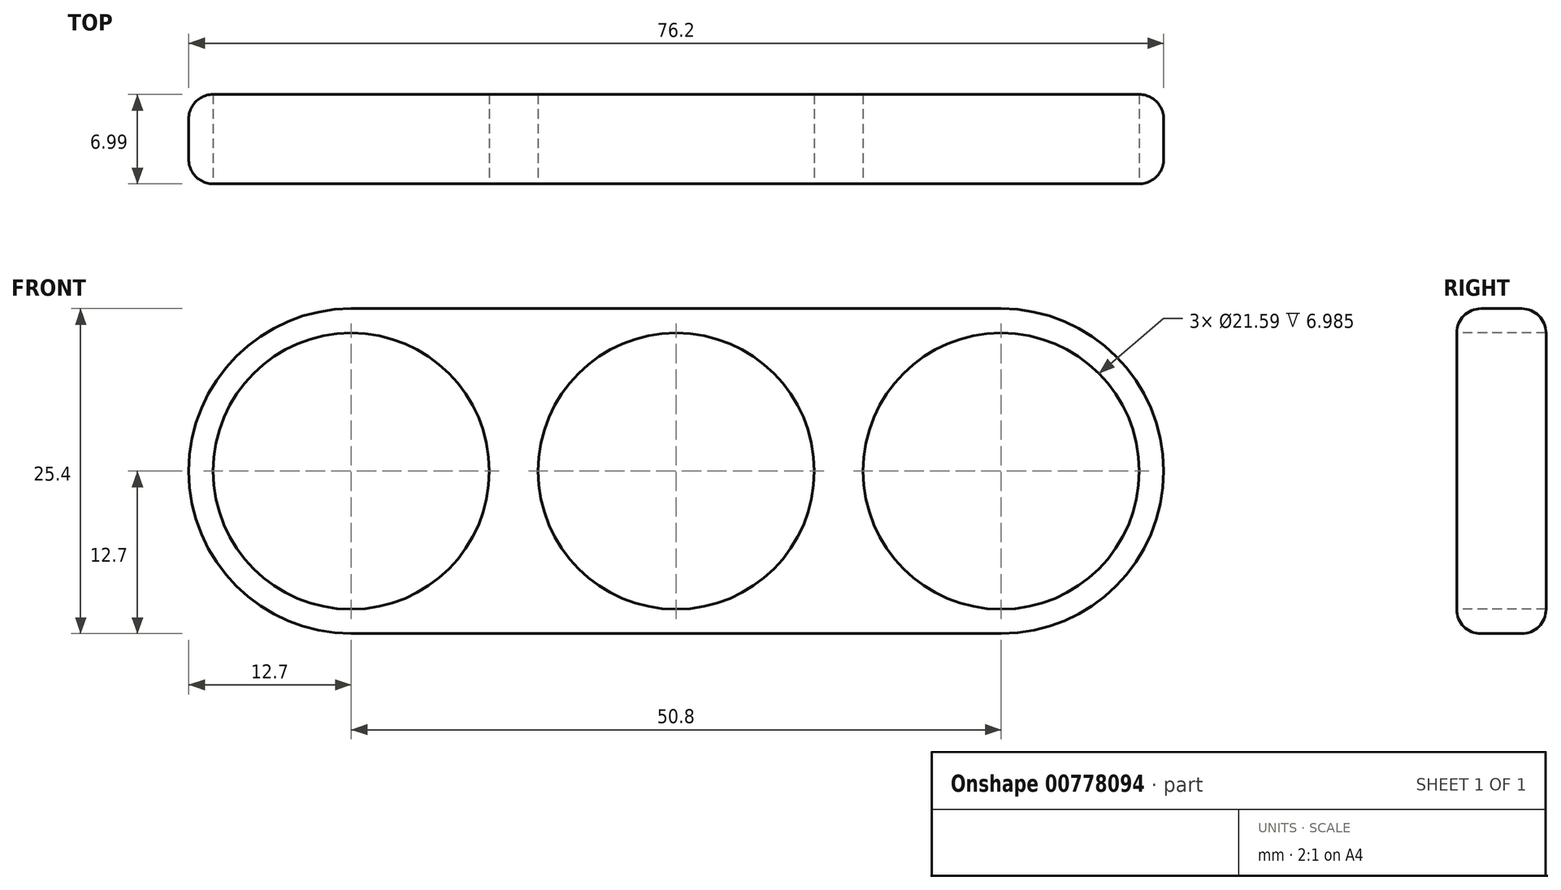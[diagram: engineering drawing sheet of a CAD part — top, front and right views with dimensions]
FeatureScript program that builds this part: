
annotation { "Feature Type Name" : "Feature", "Feature Type Description" : "" }
export const myFeature = defineFeature(function(context is Context, id is Id, definition is map)
    precondition{}
    {
        {
            var Q0;
            Q0=qCreatedBy(makeId("Front.planeOp"),FACE);
            var sketch = newSketch(context, id + "F0", { "sketchPlane" : qUnion([Q0])});
            skLineSegment(sketch, "E0", {"start": v(0, 0) * mm, "end": v(76.2, 0) * mm});
            skLineSegment(sketch, "E1", {"start": v(76.2, 0) * mm, "end": v(76.2, 25.4) * mm});
            skLineSegment(sketch, "E2", {"start": v(76.2, 25.4) * mm, "end": v(0, 25.4) * mm});
            skLineSegment(sketch, "E3", {"start": v(0, 25.4) * mm, "end": v(0, 0) * mm});
            skSolve(sketch);
        }
        {
            var Q0;
            Q0 = qSketchRegion(id + "F0", true);
            extrude(context, id + "F1", {"entities" : qUnion([Q0]), "depth" : 7 * mm, "offsetDistance" : 25.4 * mm});
        }
        {
            var Q0;
            Q0=makeQuery(id+"F1.opExtrude","SWEPT_EDGE",EDGE,{"disambiguationData":[OSD([sQuery(id+"F0.wireOp",EDGE,"E1"),sQuery(id+"F0.wireOp",EDGE,"E2")])]});
            var Q1;
            Q1=makeQuery(id+"F1.opExtrude","SWEPT_EDGE",EDGE,{"disambiguationData":[OSD([sQuery(id+"F0.wireOp",EDGE,"E2"),sQuery(id+"F0.wireOp",EDGE,"E3")])]});
            var Q2;
            Q2=makeQuery(id+"F1.opExtrude","SWEPT_EDGE",EDGE,{"disambiguationData":[OSD([sQuery(id+"F0.wireOp",EDGE,"E0"),sQuery(id+"F0.wireOp",EDGE,"E1")])]});
            var Q3;
            Q3=makeQuery(id+"F1.opExtrude","SWEPT_EDGE",EDGE,{"disambiguationData":[OSD([sQuery(id+"F0.wireOp",EDGE,"E0"),sQuery(id+"F0.wireOp",EDGE,"E3")])]});
            fillet(context, id + "F2", {"entities" : qUnion([Q0, Q1, Q2, Q3]), "radius" : 12.7 * mm, "tangentPropagation" : true, "allowEdgeOverflow" : false});
        }
        {
            var Q0;
            Q0=makeQuery(id+"F1.opExtrude","CAP_FACE",FACE,{"disambiguationData":[OSD([sQuery(id+"F0.wireOp",EDGE,"E0"),sQuery(id+"F0.wireOp",EDGE,"E1"),sQuery(id+"F0.wireOp",EDGE,"E2"),sQuery(id+"F0.wireOp",EDGE,"E3")])],"isStart":false});
            var sketch = newSketch(context, id + "F3", { "sketchPlane" : qUnion([Q0])});
            skCircle(sketch, "E4", {"center": v(12.7, 12.7) * mm, "radius": 10.8 * mm});
            skCircle(sketch, "E5", {"center": v(38.1, 12.7) * mm, "radius": 10.8 * mm});
            skCircle(sketch, "E6", {"center": v(63.5, 12.7) * mm, "radius": 10.8 * mm});
            skSolve(sketch);
        }
        {
            var Q0;
            Q0 = qSketchRegion(id + "F3", true);
            extrude(context, id + "F4", {"entities" : qUnion([Q0]), "operationType" : NewBodyOperationType.REMOVE, "endBound" : BoundingType.THROUGH_ALL, "oppositeDirection" : true, "depth" : 25.4 * mm, "offsetDistance" : 25.4 * mm});
        }
        {
            var Q0;
            Q0=makeQuery(id+"F1.opExtrude","CAP_EDGE",EDGE,{"disambiguationData":[OSD([sQuery(id+"F0.wireOp",EDGE,"E2")])],"isStart":false});
            var Q1;
            Q1=makeQuery(id+"F1.opExtrude","CAP_EDGE",EDGE,{"disambiguationData":[OSD([sQuery(id+"F0.wireOp",EDGE,"E0")])],"isStart":true});
            fillet(context, id + "F5", {"entities" : qUnion([Q0, Q1]), "radius" : 1.9 * mm, "tangentPropagation" : true, "allowEdgeOverflow" : false});
        }
    });
